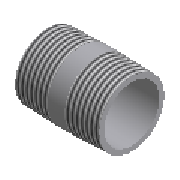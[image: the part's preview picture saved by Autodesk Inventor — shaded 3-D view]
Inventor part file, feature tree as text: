
AUTODESK INVENTOR PART (.ipt)
format: ipt  version: 2023.2 (Build 272271030, 271C)  size: 186,880 bytes
history: native  units: mm (DEFAULTED — no unit token found)
features: other x6, revolve x1, sketch x1
ambient origin geometry x8: Origin, YZ Plane, XZ Plane, XY Plane, X Axis, Y Axis, Z Axis, Center Point
bodies: Solid1 (feature_tree)
feature tree (8):
  revolve  "Revolution1"  [1 undecoded]
  other  "Work Point3"
  other  "Work Point4"
  other  "Work Axis1"
  other  "Work Point5"
  other  "Work Axis2"
  other  "Work Point6"
  sketch  "Sketch1"  dims[d12=90.0deg d1=0.312398mm d2=34.0mm d3=15.3mm d4=0.0mm d5=15.3mm d6=0.0mm d7=8.16mm d8=20.955mm d57=16.1mm d60=13.16mm d62=0.0mm]
note: 1 required parameter value undecoded (feature->parameter linkage not recoverable at this tier; creation-order binding heuristic only, values carry confidence <= 0.55)
